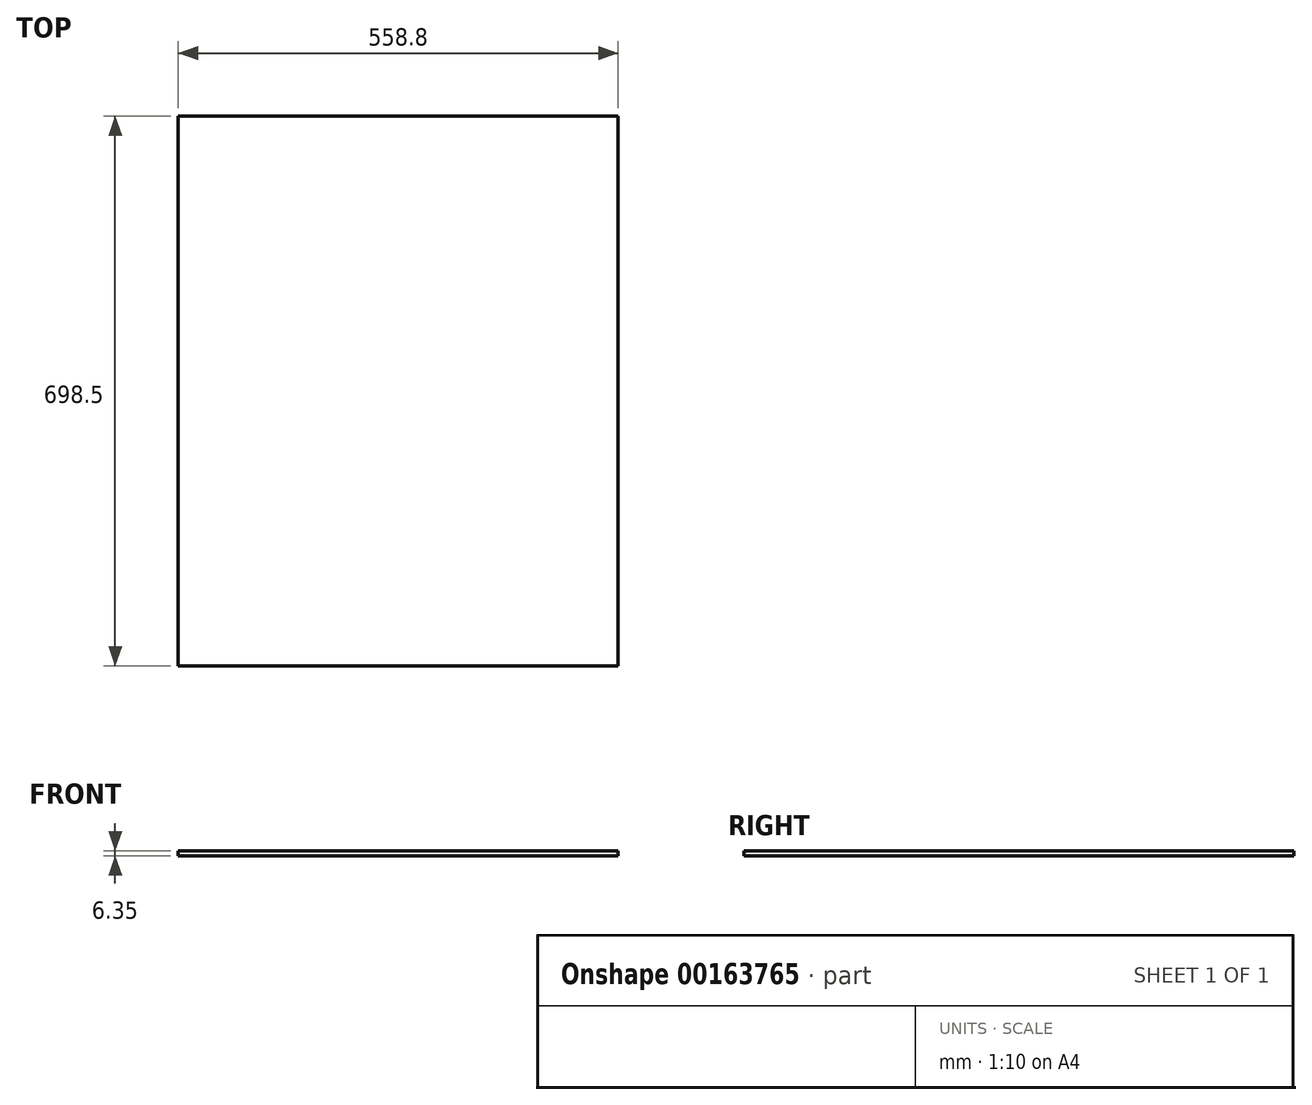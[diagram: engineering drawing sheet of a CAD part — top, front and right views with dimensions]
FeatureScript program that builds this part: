
annotation { "Feature Type Name" : "Feature", "Feature Type Description" : "" }
export const myFeature = defineFeature(function(context is Context, id is Id, definition is map)
    precondition{}
    {
        {
            var Q0;
            Q0=qCreatedBy(makeId("Top.planeOp"),FACE);
            var sketch = newSketch(context, id + "F0", { "sketchPlane" : qUnion([Q0])});
            skLineSegment(sketch, "E0.bottom", {"start": v(279.4, 349.25) * mm, "end": v(-279.4, 349.25) * mm});
            skLineSegment(sketch, "E0.top", {"start": v(279.4, -349.25) * mm, "end": v(-279.4, -349.25) * mm});
            skLineSegment(sketch, "E0.left", {"start": v(279.4, 349.25) * mm, "end": v(279.4, -349.25) * mm});
            skLineSegment(sketch, "E0.right", {"start": v(-279.4, 349.25) * mm, "end": v(-279.4, -349.25) * mm});
            skPoint(sketch, "E0.middle", {"position": v(0, 0) * mm});
            skSolve(sketch);
        }
        {
            var Q0;
            Q0 = qSketchRegion(id + "F0", true);
            extrude(context, id + "F1", {"entities" : qUnion([Q0]), "depth" : 6.35 * mm});
        }
    });
